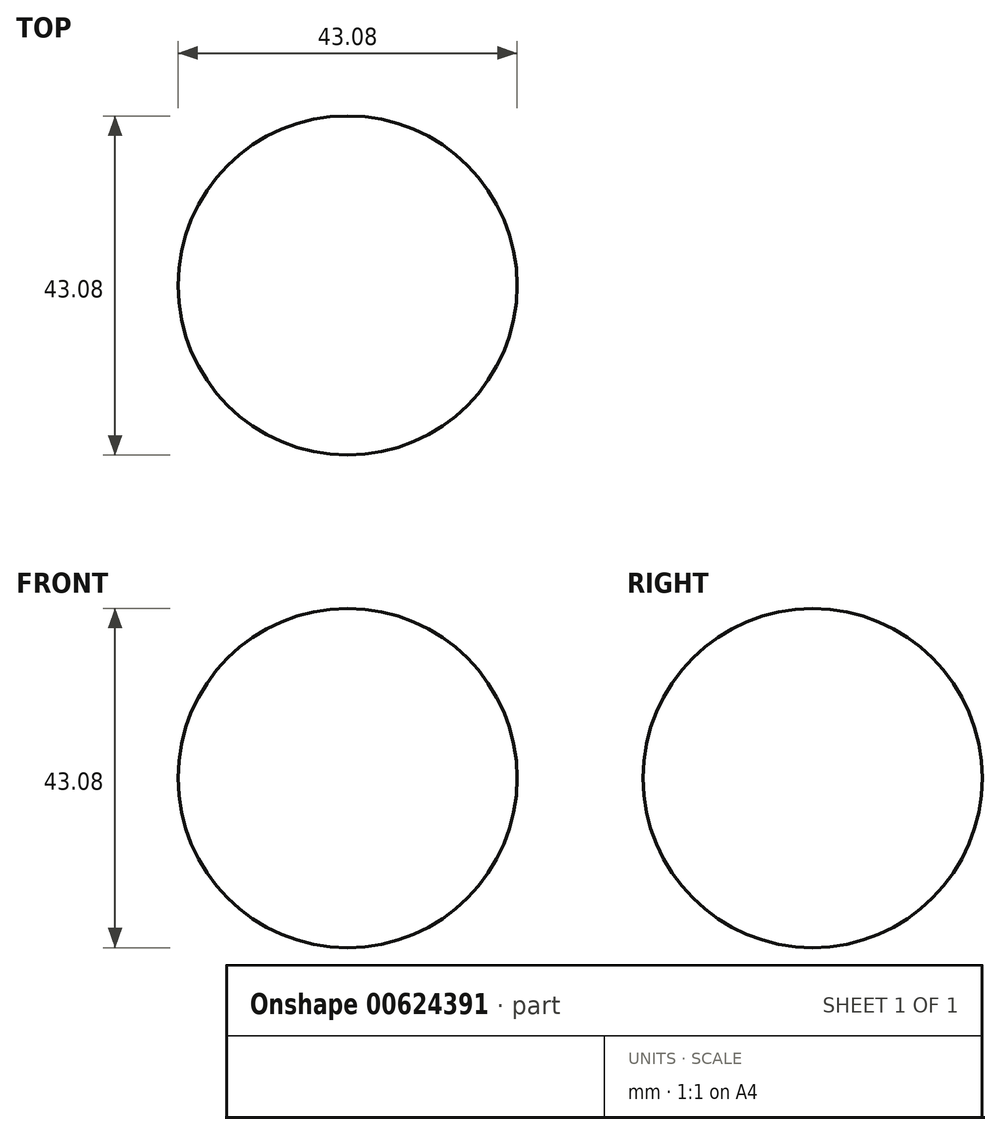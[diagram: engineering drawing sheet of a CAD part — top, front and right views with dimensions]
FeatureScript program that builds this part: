
annotation { "Feature Type Name" : "Feature", "Feature Type Description" : "" }
export const myFeature = defineFeature(function(context is Context, id is Id, definition is map)
    precondition{}
    {
        {
            var Q0;
            Q0=qCreatedBy(makeId("Front.planeOp"),FACE);
            var sketch = newSketch(context, id + "F0", { "sketchPlane" : qUnion([Q0])});
            skCircle(sketch, "E0", {"center": v(0, 0) * mm, "radius": 21.54 * mm});
            skLineSegment(sketch, "E1", {"start": v(0, 0) * mm, "end": v(45.04, 0) * mm});
            skLineSegment(sketch, "E2.MirrorCS", {"start": v(0, 0) * mm, "end": v(-45.04, 0) * mm});
            skSolve(sketch);
        }
        {
            var Q0;
            {var subQ0=sQuery(id+"F0.wireOp",EDGE,"E1");var subQ1=sQuery(id+"F0.wireOp",EDGE,"E0");var subQ2=makeQuery(id+"F0.imprint","INTERSECT",VERTEX,{"derivedFrom":[subQ1,subQ0]});Q0=makeQuery(id+"F0.imprint","IMPRINT",FACE,{"disambiguationData":[TD([[makeQuery(id+"F0.imprint","IMPRINT",EDGE,{"disambiguationData":[TD([[subQ2,1.0]])],"derivedFrom":subQ1}),1.0]])]});}
            var Q1;
            Q1=sQuery(id+"F0.wireOp",EDGE,"E1");
            revolve(context, id + "F1", {"entities" : qUnion([Q0]), "axis" : qUnion([Q1]), "revolveType" : RevolveType.FULL});
        }
    });
